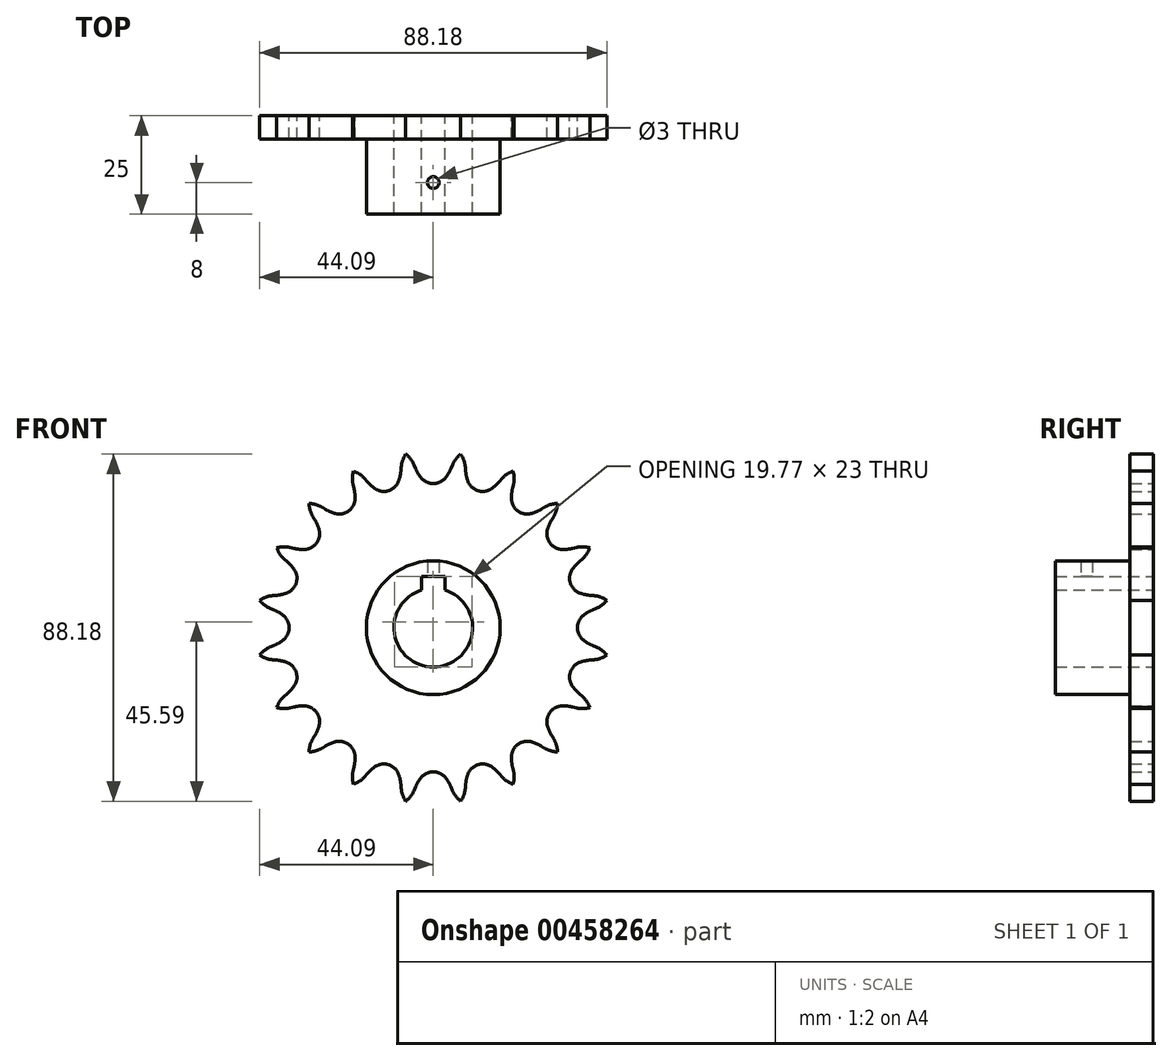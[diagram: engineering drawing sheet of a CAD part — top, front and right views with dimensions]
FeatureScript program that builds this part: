
annotation { "Feature Type Name" : "Feature", "Feature Type Description" : "" }
export const myFeature = defineFeature(function(context is Context, id is Id, definition is map)
    precondition{}
    {
        {
            var Q0;
            Q0=qCreatedBy(makeId("Front.planeOp"),FACE);
            var sketch = newSketch(context, id + "F0", { "sketchPlane" : qUnion([Q0])});
            skCircle(sketch, "E0", {"center": v(0, 0) * mm, "radius": 40.6 * mm, "construction": true});
            skLineSegment(sketch, "E1", {"start": v(0, 40.6) * mm, "end": v(73.54, 40.6) * mm, "construction": true});
            skLineSegment(sketch, "E2", {"start": v(73.54, 40.6) * mm, "end": v(-75.72, 40.6) * mm, "construction": true});
            skLineSegment(sketch, "E3", {"start": v(0, 0) * mm, "end": v(0, 40.6) * mm, "construction": true});
            skLineSegment(sketch, "E4", {"start": v(0, 82.82) * mm, "end": v(0, 40.6) * mm, "construction": true});
            skArc(sketch, "E5", {"start": v(-3.14, 38.14) * mm, "mid": v(-1.75, 37.01) * mm, "end": v(0, 36.61) * mm});
            skLineSegment(sketch, "E6", {"start": v(0, 40.6) * mm, "end": v(5, 44.5) * mm, "construction": true});
            skLineSegment(sketch, "E7", {"start": v(5, 44.5) * mm, "end": v(-4.52, 40.5) * mm, "construction": true});
            skLineSegment(sketch, "E8", {"start": v(-4.52, 40.5) * mm, "end": v(-4.9, 41.4) * mm});
            skArc(sketch, "E9", {"start": v(-4.56, 40.6) * mm, "mid": v(-3.93, 39.32) * mm, "end": v(-3.14, 38.14) * mm});
            skArc(sketch, "E10", {"start": v(-17.18, 36.78) * mm, "mid": v(-11.88, 32.36) * mm, "end": v(-5.56, 35.11) * mm});
            skLineSegment(sketch, "E11", {"start": v(0, 0) * mm, "end": v(-9.47, 59.82) * mm, "construction": true});
            skArc(sketch, "E12.trimOffspring", {"start": v(-4.9, 41.4) * mm, "mid": v(-5.76, 42.88) * mm, "end": v(-6.98, 44.09) * mm});
            skArc(sketch, "E13.trimOffspring", {"start": v(3.98, 40.4) * mm, "mid": v(3.98, 40.5) * mm, "end": v(3.98, 40.6) * mm});
            skArc(sketch, "E14.trimOffspring", {"start": v(-4.56, 40.34) * mm, "mid": v(-4.59, 40.46) * mm, "end": v(-4.62, 40.6) * mm});
            skArc(sketch, "E15.trimOffspring", {"start": v(-3.98, 40.72) * mm, "mid": v(-3.98, 40.56) * mm, "end": v(-3.98, 40.4) * mm});
            skArc(sketch, "E16.MirrorCS", {"start": v(4.9, 41.4) * mm, "mid": v(5.76, 42.88) * mm, "end": v(6.98, 44.09) * mm});
            skLineSegment(sketch, "E17.MirrorCS", {"start": v(4.52, 40.5) * mm, "end": v(4.9, 41.4) * mm});
            skArc(sketch, "E18.MirrorCS", {"start": v(4.56, 40.6) * mm, "mid": v(3.93, 39.32) * mm, "end": v(3.14, 38.14) * mm});
            skArc(sketch, "E19.MirrorCS", {"start": v(3.14, 38.14) * mm, "mid": v(1.75, 37.01) * mm, "end": v(0, 36.61) * mm});
            skArc(sketch, "E20.1.0", {"start": v(-17.45, 37.86) * mm, "mid": v(-18.73, 39) * mm, "end": v(-20.26, 39.77) * mm});
            skLineSegment(sketch, "E20.1.1", {"start": v(-16.81, 37.12) * mm, "end": v(-17.45, 37.86) * mm});
            skArc(sketch, "E20.1.2", {"start": v(-16.88, 37.2) * mm, "mid": v(-15.89, 36.18) * mm, "end": v(-14.77, 35.3) * mm});
            skArc(sketch, "E20.1.3", {"start": v(-14.77, 35.3) * mm, "mid": v(-13.1, 34.66) * mm, "end": v(-11.31, 34.82) * mm});
            skArc(sketch, "E20.1.4", {"start": v(-8.8, 37.24) * mm, "mid": v(-9.78, 35.74) * mm, "end": v(-11.31, 34.82) * mm});
            skArc(sketch, "E20.1.5", {"start": v(-8.2, 40.01) * mm, "mid": v(-8.4, 38.6) * mm, "end": v(-8.8, 37.24) * mm});
            skLineSegment(sketch, "E20.1.6", {"start": v(-8.22, 39.9) * mm, "end": v(-8.13, 40.89) * mm});
            skArc(sketch, "E20.1.7", {"start": v(-8.13, 40.89) * mm, "mid": v(-7.77, 42.56) * mm, "end": v(-6.98, 44.09) * mm});
            skArc(sketch, "E20.2.0", {"start": v(-28.3, 30.61) * mm, "mid": v(-29.87, 31.3) * mm, "end": v(-31.56, 31.56) * mm});
            skLineSegment(sketch, "E20.2.1", {"start": v(-27.46, 30.1) * mm, "end": v(-28.3, 30.61) * mm});
            skArc(sketch, "E20.2.2", {"start": v(-27.55, 30.16) * mm, "mid": v(-26.3, 29.5) * mm, "end": v(-24.96, 29.01) * mm});
            skArc(sketch, "E20.2.3", {"start": v(-24.96, 29.01) * mm, "mid": v(-23.17, 28.92) * mm, "end": v(-21.52, 29.62) * mm});
            skArc(sketch, "E20.2.4", {"start": v(-19.88, 32.7) * mm, "mid": v(-20.34, 30.97) * mm, "end": v(-21.52, 29.62) * mm});
            skArc(sketch, "E20.2.5", {"start": v(-20.17, 35.52) * mm, "mid": v(-19.93, 34.12) * mm, "end": v(-19.88, 32.7) * mm});
            skLineSegment(sketch, "E20.2.6", {"start": v(-20.15, 35.42) * mm, "end": v(-20.37, 36.37) * mm});
            skArc(sketch, "E20.2.7", {"start": v(-20.37, 36.37) * mm, "mid": v(-20.54, 38.08) * mm, "end": v(-20.26, 39.77) * mm});
            skArc(sketch, "E20.3.0", {"start": v(-36.37, 20.37) * mm, "mid": v(-38.08, 20.54) * mm, "end": v(-39.77, 20.26) * mm});
            skLineSegment(sketch, "E20.3.1", {"start": v(-35.42, 20.15) * mm, "end": v(-36.37, 20.37) * mm});
            skArc(sketch, "E20.3.2", {"start": v(-35.52, 20.17) * mm, "mid": v(-34.12, 19.93) * mm, "end": v(-32.7, 19.88) * mm});
            skArc(sketch, "E20.3.3", {"start": v(-32.7, 19.88) * mm, "mid": v(-30.97, 20.34) * mm, "end": v(-29.62, 21.52) * mm});
            skArc(sketch, "E20.3.4", {"start": v(-29.01, 24.96) * mm, "mid": v(-28.92, 23.17) * mm, "end": v(-29.62, 21.52) * mm});
            skArc(sketch, "E20.3.5", {"start": v(-30.16, 27.55) * mm, "mid": v(-29.5, 26.3) * mm, "end": v(-29.01, 24.96) * mm});
            skLineSegment(sketch, "E20.3.6", {"start": v(-30.1, 27.46) * mm, "end": v(-30.61, 28.3) * mm});
            skArc(sketch, "E20.3.7", {"start": v(-30.61, 28.3) * mm, "mid": v(-31.3, 29.87) * mm, "end": v(-31.56, 31.56) * mm});
            skArc(sketch, "E20.4.0", {"start": v(-40.89, 8.13) * mm, "mid": v(-42.56, 7.77) * mm, "end": v(-44.09, 6.98) * mm});
            skLineSegment(sketch, "E20.4.1", {"start": v(-39.9, 8.22) * mm, "end": v(-40.89, 8.13) * mm});
            skArc(sketch, "E20.4.2", {"start": v(-40.01, 8.2) * mm, "mid": v(-38.6, 8.4) * mm, "end": v(-37.24, 8.8) * mm});
            skArc(sketch, "E20.4.3", {"start": v(-37.24, 8.8) * mm, "mid": v(-35.74, 9.78) * mm, "end": v(-34.82, 11.31) * mm});
            skArc(sketch, "E20.4.4", {"start": v(-35.3, 14.77) * mm, "mid": v(-34.66, 13.1) * mm, "end": v(-34.82, 11.31) * mm});
            skArc(sketch, "E20.4.5", {"start": v(-37.2, 16.88) * mm, "mid": v(-36.18, 15.89) * mm, "end": v(-35.3, 14.77) * mm});
            skLineSegment(sketch, "E20.4.6", {"start": v(-37.12, 16.81) * mm, "end": v(-37.86, 17.45) * mm});
            skArc(sketch, "E20.4.7", {"start": v(-37.86, 17.45) * mm, "mid": v(-39, 18.73) * mm, "end": v(-39.77, 20.26) * mm});
            skArc(sketch, "E20.5.0", {"start": v(-41.4, -4.9) * mm, "mid": v(-42.88, -5.76) * mm, "end": v(-44.09, -6.98) * mm});
            skLineSegment(sketch, "E20.5.1", {"start": v(-40.5, -4.52) * mm, "end": v(-41.4, -4.9) * mm});
            skArc(sketch, "E20.5.2", {"start": v(-40.6, -4.56) * mm, "mid": v(-39.32, -3.93) * mm, "end": v(-38.14, -3.14) * mm});
            skArc(sketch, "E20.5.3", {"start": v(-38.14, -3.14) * mm, "mid": v(-37.01, -1.75) * mm, "end": v(-36.61, 0) * mm});
            skArc(sketch, "E20.5.4", {"start": v(-38.14, 3.14) * mm, "mid": v(-37.01, 1.75) * mm, "end": v(-36.61, 0) * mm});
            skArc(sketch, "E20.5.5", {"start": v(-40.6, 4.56) * mm, "mid": v(-39.32, 3.93) * mm, "end": v(-38.14, 3.14) * mm});
            skLineSegment(sketch, "E20.5.6", {"start": v(-40.5, 4.52) * mm, "end": v(-41.4, 4.9) * mm});
            skArc(sketch, "E20.5.7", {"start": v(-41.4, 4.9) * mm, "mid": v(-42.88, 5.76) * mm, "end": v(-44.09, 6.98) * mm});
            skArc(sketch, "E20.6.0", {"start": v(-37.86, -17.45) * mm, "mid": v(-39, -18.73) * mm, "end": v(-39.77, -20.26) * mm});
            skLineSegment(sketch, "E20.6.1", {"start": v(-37.12, -16.81) * mm, "end": v(-37.86, -17.45) * mm});
            skArc(sketch, "E20.6.2", {"start": v(-37.2, -16.88) * mm, "mid": v(-36.18, -15.89) * mm, "end": v(-35.3, -14.77) * mm});
            skArc(sketch, "E20.6.3", {"start": v(-35.3, -14.77) * mm, "mid": v(-34.66, -13.1) * mm, "end": v(-34.82, -11.31) * mm});
            skArc(sketch, "E20.6.4", {"start": v(-37.24, -8.8) * mm, "mid": v(-35.74, -9.78) * mm, "end": v(-34.82, -11.31) * mm});
            skArc(sketch, "E20.6.5", {"start": v(-40.01, -8.2) * mm, "mid": v(-38.6, -8.4) * mm, "end": v(-37.24, -8.8) * mm});
            skLineSegment(sketch, "E20.6.6", {"start": v(-39.9, -8.22) * mm, "end": v(-40.89, -8.13) * mm});
            skArc(sketch, "E20.6.7", {"start": v(-40.89, -8.13) * mm, "mid": v(-42.56, -7.77) * mm, "end": v(-44.09, -6.98) * mm});
            skArc(sketch, "E20.7.0", {"start": v(-30.61, -28.3) * mm, "mid": v(-31.3, -29.87) * mm, "end": v(-31.56, -31.56) * mm});
            skLineSegment(sketch, "E20.7.1", {"start": v(-30.1, -27.46) * mm, "end": v(-30.61, -28.3) * mm});
            skArc(sketch, "E20.7.2", {"start": v(-30.16, -27.55) * mm, "mid": v(-29.5, -26.3) * mm, "end": v(-29.01, -24.96) * mm});
            skArc(sketch, "E20.7.3", {"start": v(-29.01, -24.96) * mm, "mid": v(-28.92, -23.17) * mm, "end": v(-29.62, -21.52) * mm});
            skArc(sketch, "E20.7.4", {"start": v(-32.7, -19.88) * mm, "mid": v(-30.97, -20.34) * mm, "end": v(-29.62, -21.52) * mm});
            skArc(sketch, "E20.7.5", {"start": v(-35.52, -20.17) * mm, "mid": v(-34.12, -19.93) * mm, "end": v(-32.7, -19.88) * mm});
            skLineSegment(sketch, "E20.7.6", {"start": v(-35.42, -20.15) * mm, "end": v(-36.37, -20.37) * mm});
            skArc(sketch, "E20.7.7", {"start": v(-36.37, -20.37) * mm, "mid": v(-38.08, -20.54) * mm, "end": v(-39.77, -20.26) * mm});
            skArc(sketch, "E20.8.0", {"start": v(-20.37, -36.37) * mm, "mid": v(-20.54, -38.08) * mm, "end": v(-20.26, -39.77) * mm});
            skLineSegment(sketch, "E20.8.1", {"start": v(-20.15, -35.42) * mm, "end": v(-20.37, -36.37) * mm});
            skArc(sketch, "E20.8.2", {"start": v(-20.17, -35.52) * mm, "mid": v(-19.93, -34.12) * mm, "end": v(-19.88, -32.7) * mm});
            skArc(sketch, "E20.8.3", {"start": v(-19.88, -32.7) * mm, "mid": v(-20.34, -30.97) * mm, "end": v(-21.52, -29.62) * mm});
            skArc(sketch, "E20.8.4", {"start": v(-24.96, -29.01) * mm, "mid": v(-23.17, -28.92) * mm, "end": v(-21.52, -29.62) * mm});
            skArc(sketch, "E20.8.5", {"start": v(-27.55, -30.16) * mm, "mid": v(-26.3, -29.5) * mm, "end": v(-24.96, -29.01) * mm});
            skLineSegment(sketch, "E20.8.6", {"start": v(-27.46, -30.1) * mm, "end": v(-28.3, -30.61) * mm});
            skArc(sketch, "E20.8.7", {"start": v(-28.3, -30.61) * mm, "mid": v(-29.87, -31.3) * mm, "end": v(-31.56, -31.56) * mm});
            skArc(sketch, "E20.9.0", {"start": v(-8.13, -40.89) * mm, "mid": v(-7.77, -42.56) * mm, "end": v(-6.98, -44.09) * mm});
            skLineSegment(sketch, "E20.9.1", {"start": v(-8.22, -39.9) * mm, "end": v(-8.13, -40.89) * mm});
            skArc(sketch, "E20.9.2", {"start": v(-8.2, -40.01) * mm, "mid": v(-8.4, -38.6) * mm, "end": v(-8.8, -37.24) * mm});
            skArc(sketch, "E20.9.3", {"start": v(-8.8, -37.24) * mm, "mid": v(-9.78, -35.74) * mm, "end": v(-11.31, -34.82) * mm});
            skArc(sketch, "E20.9.4", {"start": v(-14.77, -35.3) * mm, "mid": v(-13.1, -34.66) * mm, "end": v(-11.31, -34.82) * mm});
            skArc(sketch, "E20.9.5", {"start": v(-16.88, -37.2) * mm, "mid": v(-15.89, -36.18) * mm, "end": v(-14.77, -35.3) * mm});
            skLineSegment(sketch, "E20.9.6", {"start": v(-16.81, -37.12) * mm, "end": v(-17.45, -37.86) * mm});
            skArc(sketch, "E20.9.7", {"start": v(-17.45, -37.86) * mm, "mid": v(-18.73, -39) * mm, "end": v(-20.26, -39.77) * mm});
            skArc(sketch, "E20.10.0", {"start": v(4.9, -41.4) * mm, "mid": v(5.76, -42.88) * mm, "end": v(6.98, -44.09) * mm});
            skLineSegment(sketch, "E20.10.1", {"start": v(4.52, -40.5) * mm, "end": v(4.9, -41.4) * mm});
            skArc(sketch, "E20.10.2", {"start": v(4.56, -40.6) * mm, "mid": v(3.93, -39.32) * mm, "end": v(3.14, -38.14) * mm});
            skArc(sketch, "E20.10.3", {"start": v(3.14, -38.14) * mm, "mid": v(1.75, -37.01) * mm, "end": v(0, -36.61) * mm});
            skArc(sketch, "E20.10.4", {"start": v(-3.14, -38.14) * mm, "mid": v(-1.75, -37.01) * mm, "end": v(0, -36.61) * mm});
            skArc(sketch, "E20.10.5", {"start": v(-4.56, -40.6) * mm, "mid": v(-3.93, -39.32) * mm, "end": v(-3.14, -38.14) * mm});
            skLineSegment(sketch, "E20.10.6", {"start": v(-4.52, -40.5) * mm, "end": v(-4.9, -41.4) * mm});
            skArc(sketch, "E20.10.7", {"start": v(-4.9, -41.4) * mm, "mid": v(-5.76, -42.88) * mm, "end": v(-6.98, -44.09) * mm});
            skArc(sketch, "E20.11.0", {"start": v(17.45, -37.86) * mm, "mid": v(18.73, -39) * mm, "end": v(20.26, -39.77) * mm});
            skLineSegment(sketch, "E20.11.1", {"start": v(16.81, -37.12) * mm, "end": v(17.45, -37.86) * mm});
            skArc(sketch, "E20.11.2", {"start": v(16.88, -37.2) * mm, "mid": v(15.89, -36.18) * mm, "end": v(14.77, -35.3) * mm});
            skArc(sketch, "E20.11.3", {"start": v(14.77, -35.3) * mm, "mid": v(13.1, -34.66) * mm, "end": v(11.31, -34.82) * mm});
            skArc(sketch, "E20.11.4", {"start": v(8.8, -37.24) * mm, "mid": v(9.78, -35.74) * mm, "end": v(11.31, -34.82) * mm});
            skArc(sketch, "E20.11.5", {"start": v(8.2, -40.01) * mm, "mid": v(8.4, -38.6) * mm, "end": v(8.8, -37.24) * mm});
            skLineSegment(sketch, "E20.11.6", {"start": v(8.22, -39.9) * mm, "end": v(8.13, -40.89) * mm});
            skArc(sketch, "E20.11.7", {"start": v(8.13, -40.89) * mm, "mid": v(7.77, -42.56) * mm, "end": v(6.98, -44.09) * mm});
            skArc(sketch, "E20.12.0", {"start": v(28.3, -30.61) * mm, "mid": v(29.87, -31.3) * mm, "end": v(31.56, -31.56) * mm});
            skLineSegment(sketch, "E20.12.1", {"start": v(27.46, -30.1) * mm, "end": v(28.3, -30.61) * mm});
            skArc(sketch, "E20.12.2", {"start": v(27.55, -30.16) * mm, "mid": v(26.3, -29.5) * mm, "end": v(24.96, -29.01) * mm});
            skArc(sketch, "E20.12.3", {"start": v(24.96, -29.01) * mm, "mid": v(23.17, -28.92) * mm, "end": v(21.52, -29.62) * mm});
            skArc(sketch, "E20.12.4", {"start": v(19.88, -32.7) * mm, "mid": v(20.34, -30.97) * mm, "end": v(21.52, -29.62) * mm});
            skArc(sketch, "E20.12.5", {"start": v(20.17, -35.52) * mm, "mid": v(19.93, -34.12) * mm, "end": v(19.88, -32.7) * mm});
            skLineSegment(sketch, "E20.12.6", {"start": v(20.15, -35.42) * mm, "end": v(20.37, -36.37) * mm});
            skArc(sketch, "E20.12.7", {"start": v(20.37, -36.37) * mm, "mid": v(20.54, -38.08) * mm, "end": v(20.26, -39.77) * mm});
            skArc(sketch, "E20.13.0", {"start": v(36.37, -20.37) * mm, "mid": v(38.08, -20.54) * mm, "end": v(39.77, -20.26) * mm});
            skLineSegment(sketch, "E20.13.1", {"start": v(35.42, -20.15) * mm, "end": v(36.37, -20.37) * mm});
            skArc(sketch, "E20.13.2", {"start": v(35.52, -20.17) * mm, "mid": v(34.12, -19.93) * mm, "end": v(32.7, -19.88) * mm});
            skArc(sketch, "E20.13.3", {"start": v(32.7, -19.88) * mm, "mid": v(30.97, -20.34) * mm, "end": v(29.62, -21.52) * mm});
            skArc(sketch, "E20.13.4", {"start": v(29.01, -24.96) * mm, "mid": v(28.92, -23.17) * mm, "end": v(29.62, -21.52) * mm});
            skArc(sketch, "E20.13.5", {"start": v(30.16, -27.55) * mm, "mid": v(29.5, -26.3) * mm, "end": v(29.01, -24.96) * mm});
            skLineSegment(sketch, "E20.13.6", {"start": v(30.1, -27.46) * mm, "end": v(30.61, -28.3) * mm});
            skArc(sketch, "E20.13.7", {"start": v(30.61, -28.3) * mm, "mid": v(31.3, -29.87) * mm, "end": v(31.56, -31.56) * mm});
            skArc(sketch, "E20.14.0", {"start": v(40.89, -8.13) * mm, "mid": v(42.56, -7.77) * mm, "end": v(44.09, -6.98) * mm});
            skLineSegment(sketch, "E20.14.1", {"start": v(39.9, -8.22) * mm, "end": v(40.89, -8.13) * mm});
            skArc(sketch, "E20.14.2", {"start": v(40.01, -8.2) * mm, "mid": v(38.6, -8.4) * mm, "end": v(37.24, -8.8) * mm});
            skArc(sketch, "E20.14.3", {"start": v(37.24, -8.8) * mm, "mid": v(35.74, -9.78) * mm, "end": v(34.82, -11.31) * mm});
            skArc(sketch, "E20.14.4", {"start": v(35.3, -14.77) * mm, "mid": v(34.66, -13.1) * mm, "end": v(34.82, -11.31) * mm});
            skArc(sketch, "E20.14.5", {"start": v(37.2, -16.88) * mm, "mid": v(36.18, -15.89) * mm, "end": v(35.3, -14.77) * mm});
            skLineSegment(sketch, "E20.14.6", {"start": v(37.12, -16.81) * mm, "end": v(37.86, -17.45) * mm});
            skArc(sketch, "E20.14.7", {"start": v(37.86, -17.45) * mm, "mid": v(39, -18.73) * mm, "end": v(39.77, -20.26) * mm});
            skArc(sketch, "E20.15.0", {"start": v(41.4, 4.9) * mm, "mid": v(42.88, 5.76) * mm, "end": v(44.09, 6.98) * mm});
            skLineSegment(sketch, "E20.15.1", {"start": v(40.5, 4.52) * mm, "end": v(41.4, 4.9) * mm});
            skArc(sketch, "E20.15.2", {"start": v(40.6, 4.56) * mm, "mid": v(39.32, 3.93) * mm, "end": v(38.14, 3.14) * mm});
            skArc(sketch, "E20.15.3", {"start": v(38.14, 3.14) * mm, "mid": v(37.01, 1.75) * mm, "end": v(36.61, 0) * mm});
            skArc(sketch, "E20.15.4", {"start": v(38.14, -3.14) * mm, "mid": v(37.01, -1.75) * mm, "end": v(36.61, 0) * mm});
            skArc(sketch, "E20.15.5", {"start": v(40.6, -4.56) * mm, "mid": v(39.32, -3.93) * mm, "end": v(38.14, -3.14) * mm});
            skLineSegment(sketch, "E20.15.6", {"start": v(40.5, -4.52) * mm, "end": v(41.4, -4.9) * mm});
            skArc(sketch, "E20.15.7", {"start": v(41.4, -4.9) * mm, "mid": v(42.88, -5.76) * mm, "end": v(44.09, -6.98) * mm});
            skArc(sketch, "E20.16.0", {"start": v(37.86, 17.45) * mm, "mid": v(39, 18.73) * mm, "end": v(39.77, 20.26) * mm});
            skLineSegment(sketch, "E20.16.1", {"start": v(37.12, 16.81) * mm, "end": v(37.86, 17.45) * mm});
            skArc(sketch, "E20.16.2", {"start": v(37.2, 16.88) * mm, "mid": v(36.18, 15.89) * mm, "end": v(35.3, 14.77) * mm});
            skArc(sketch, "E20.16.3", {"start": v(35.3, 14.77) * mm, "mid": v(34.66, 13.1) * mm, "end": v(34.82, 11.31) * mm});
            skArc(sketch, "E20.16.4", {"start": v(37.24, 8.8) * mm, "mid": v(35.74, 9.78) * mm, "end": v(34.82, 11.31) * mm});
            skArc(sketch, "E20.16.5", {"start": v(40.01, 8.2) * mm, "mid": v(38.6, 8.4) * mm, "end": v(37.24, 8.8) * mm});
            skLineSegment(sketch, "E20.16.6", {"start": v(39.9, 8.22) * mm, "end": v(40.89, 8.13) * mm});
            skArc(sketch, "E20.16.7", {"start": v(40.89, 8.13) * mm, "mid": v(42.56, 7.77) * mm, "end": v(44.09, 6.98) * mm});
            skArc(sketch, "E20.17.0", {"start": v(30.61, 28.3) * mm, "mid": v(31.3, 29.87) * mm, "end": v(31.56, 31.56) * mm});
            skLineSegment(sketch, "E20.17.1", {"start": v(30.1, 27.46) * mm, "end": v(30.61, 28.3) * mm});
            skArc(sketch, "E20.17.2", {"start": v(30.16, 27.55) * mm, "mid": v(29.5, 26.3) * mm, "end": v(29.01, 24.96) * mm});
            skArc(sketch, "E20.17.3", {"start": v(29.01, 24.96) * mm, "mid": v(28.92, 23.17) * mm, "end": v(29.62, 21.52) * mm});
            skArc(sketch, "E20.17.4", {"start": v(32.7, 19.88) * mm, "mid": v(30.97, 20.34) * mm, "end": v(29.62, 21.52) * mm});
            skArc(sketch, "E20.17.5", {"start": v(35.52, 20.17) * mm, "mid": v(34.12, 19.93) * mm, "end": v(32.7, 19.88) * mm});
            skLineSegment(sketch, "E20.17.6", {"start": v(35.42, 20.15) * mm, "end": v(36.37, 20.37) * mm});
            skArc(sketch, "E20.17.7", {"start": v(36.37, 20.37) * mm, "mid": v(38.08, 20.54) * mm, "end": v(39.77, 20.26) * mm});
            skArc(sketch, "E20.18.0", {"start": v(20.37, 36.37) * mm, "mid": v(20.54, 38.08) * mm, "end": v(20.26, 39.77) * mm});
            skLineSegment(sketch, "E20.18.1", {"start": v(20.15, 35.42) * mm, "end": v(20.37, 36.37) * mm});
            skArc(sketch, "E20.18.2", {"start": v(20.17, 35.52) * mm, "mid": v(19.93, 34.12) * mm, "end": v(19.88, 32.7) * mm});
            skArc(sketch, "E20.18.3", {"start": v(19.88, 32.7) * mm, "mid": v(20.34, 30.97) * mm, "end": v(21.52, 29.62) * mm});
            skArc(sketch, "E20.18.4", {"start": v(24.96, 29.01) * mm, "mid": v(23.17, 28.92) * mm, "end": v(21.52, 29.62) * mm});
            skArc(sketch, "E20.18.5", {"start": v(27.55, 30.16) * mm, "mid": v(26.3, 29.5) * mm, "end": v(24.96, 29.01) * mm});
            skLineSegment(sketch, "E20.18.6", {"start": v(27.46, 30.1) * mm, "end": v(28.3, 30.61) * mm});
            skArc(sketch, "E20.18.7", {"start": v(28.3, 30.61) * mm, "mid": v(29.87, 31.3) * mm, "end": v(31.56, 31.56) * mm});
            skArc(sketch, "E20.19.0", {"start": v(8.13, 40.89) * mm, "mid": v(7.77, 42.56) * mm, "end": v(6.98, 44.09) * mm});
            skLineSegment(sketch, "E20.19.1", {"start": v(8.22, 39.9) * mm, "end": v(8.13, 40.89) * mm});
            skArc(sketch, "E20.19.2", {"start": v(8.2, 40.01) * mm, "mid": v(8.4, 38.6) * mm, "end": v(8.8, 37.24) * mm});
            skArc(sketch, "E20.19.3", {"start": v(8.8, 37.24) * mm, "mid": v(9.78, 35.74) * mm, "end": v(11.31, 34.82) * mm});
            skArc(sketch, "E20.19.4", {"start": v(14.77, 35.3) * mm, "mid": v(13.1, 34.66) * mm, "end": v(11.31, 34.82) * mm});
            skArc(sketch, "E20.19.5", {"start": v(16.88, 37.2) * mm, "mid": v(15.89, 36.18) * mm, "end": v(14.77, 35.3) * mm});
            skLineSegment(sketch, "E20.19.6", {"start": v(16.81, 37.12) * mm, "end": v(17.45, 37.86) * mm});
            skArc(sketch, "E20.19.7", {"start": v(17.45, 37.86) * mm, "mid": v(18.73, 39) * mm, "end": v(20.26, 39.77) * mm});
            skSolve(sketch);
        }
        {
            var Q0;
            Q0=qCreatedBy(makeId("Front.planeOp"),FACE);
            var sketch = newSketch(context, id + "F1", { "sketchPlane" : qUnion([Q0])});
            skCircle(sketch, "E21", {"center": v(0, 0) * mm, "radius": 17 * mm});
            skSolve(sketch);
        }
        {
            var Q0;
            Q0 = qSketchRegion(id + "F1", true);
            extrude(context, id + "F2", {"entities" : qUnion([Q0]), "depth" : 25 * mm, "offsetDistance" : 25 * mm});
        }
        {
            var Q0;
            {var subQ50=sQuery(id+"F0.wireOp",EDGE,"E5");Q0=makeQuery(id+"F0.imprint","IMPRINT",FACE,{"disambiguationData":[TD([[makeQuery(id+"F0.imprint","IMPRINT",EDGE,{"derivedFrom":subQ50}),-1.0]])]});}
            extrude(context, id + "F3", {"entities" : qUnion([Q0]), "operationType" : NewBodyOperationType.ADD, "depth" : 6 * mm, "offsetDistance" : 25 * mm});
        }
        {
            var Q0;
            Q0=qCreatedBy(makeId("Front.planeOp"),FACE);
            var sketch = newSketch(context, id + "F4", { "sketchPlane" : qUnion([Q0])});
            skLineSegment(sketch, "E22.bottom", {"start": v(-3, 0) * mm, "end": v(3, 0) * mm});
            skLineSegment(sketch, "E22.top", {"start": v(-3, 13) * mm, "end": v(3, 13) * mm});
            skLineSegment(sketch, "E22.left", {"start": v(-3, 0) * mm, "end": v(-3, 13) * mm});
            skLineSegment(sketch, "E22.right", {"start": v(3, 0) * mm, "end": v(3, 13) * mm});
            skSolve(sketch);
        }
        {
            var Q0;
            Q0 = qSketchRegion(id + "F4", true);
            extrude(context, id + "F5", {"entities" : qUnion([Q0]), "operationType" : NewBodyOperationType.REMOVE, "depth" : 25 * mm, "offsetDistance" : 25 * mm});
        }
        {
            var Q0;
            Q0=qCreatedBy(makeId("Front.planeOp"),FACE);
            var sketch = newSketch(context, id + "F6", { "sketchPlane" : qUnion([Q0])});
            skCircle(sketch, "E23", {"center": v(0, 0) * mm, "radius": 10 * mm});
            skSolve(sketch);
        }
        {
            var Q0;
            Q0 = qSketchRegion(id + "F6", true);
            extrude(context, id + "F7", {"entities" : qUnion([Q0]), "operationType" : NewBodyOperationType.REMOVE, "depth" : 25 * mm, "offsetDistance" : 25 * mm});
        }
        {
            var Q0;
            Q0=qCreatedBy(makeId("Top.planeOp"),FACE);
            var sketch = newSketch(context, id + "F8", { "sketchPlane" : qUnion([Q0])});
            skCircle(sketch, "E24", {"center": v(0, -17) * mm, "radius": 1.5 * mm});
            skSolve(sketch);
        }
        {
            var Q0;
            Q0 = qSketchRegion(id + "F8", true);
            extrude(context, id + "F9", {"entities" : qUnion([Q0]), "operationType" : NewBodyOperationType.REMOVE, "depth" : 25 * mm, "offsetDistance" : 25 * mm});
        }
    });
